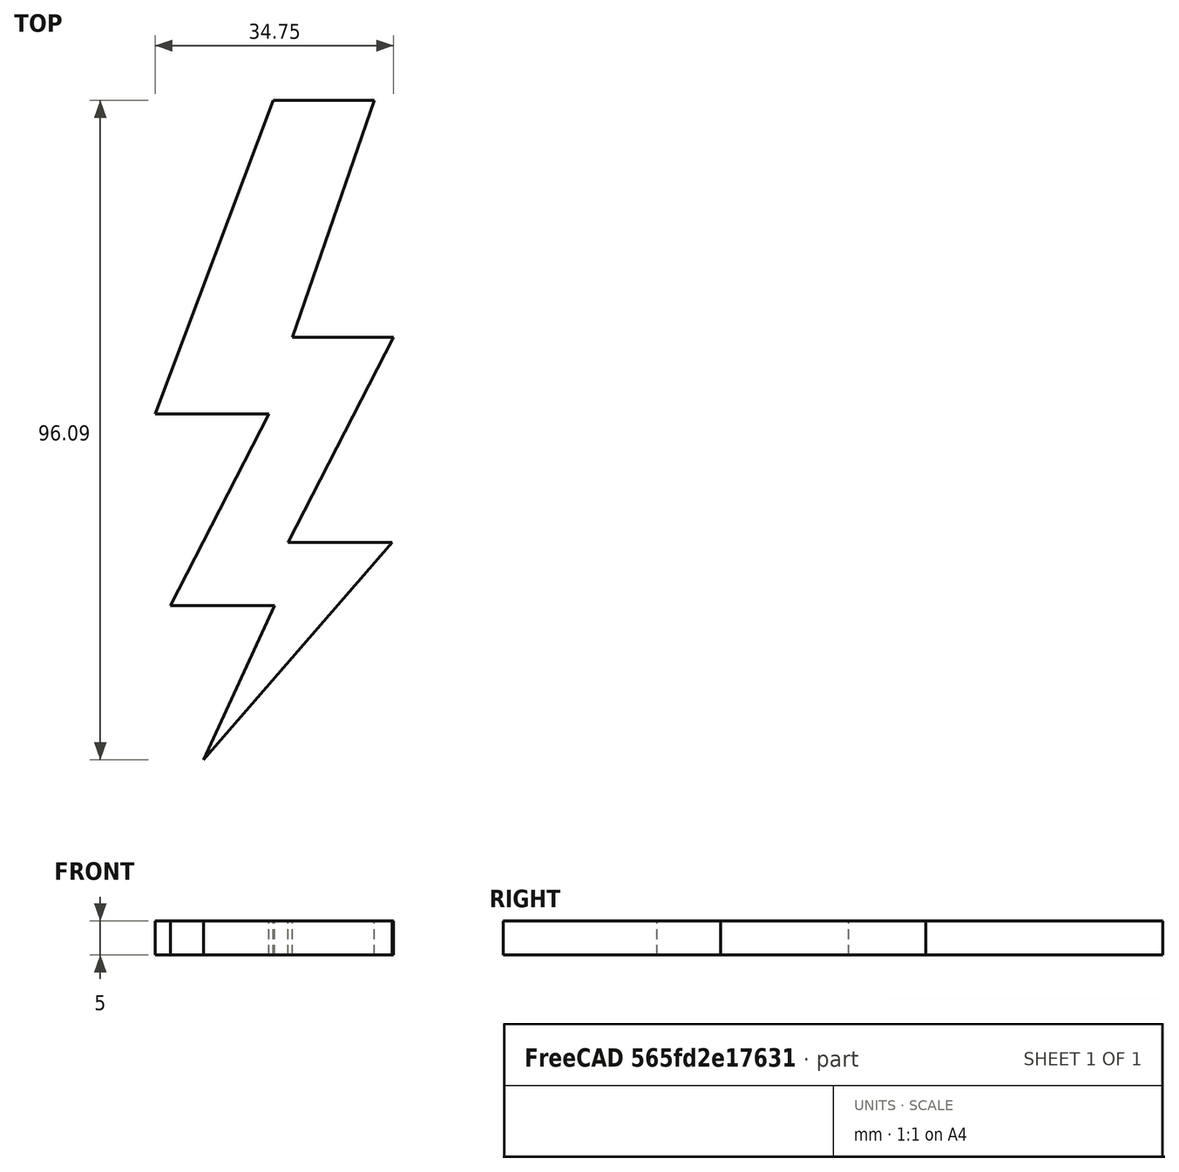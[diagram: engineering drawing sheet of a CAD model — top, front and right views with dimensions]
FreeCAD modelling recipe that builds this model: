
FCSTD DOCUMENT  (FreeCAD 0.21R33694 (Git))
Label: OJT1_T16R03.team_llamp
License: All rights reserved
LicenseURL: http://en.wikipedia.org/wiki/All_rights_reserved
objects: Sketcher::SketchObject×1, PartDesign::Pad×1, PartDesign::Body×1
note: 4 computed .brp shape members not serialized (recipe doc carries the construction recipe); baked Part::Feature solids carry a one-line shape summary decoded from their .brp

FEATURE [Sketcher::SketchObject] Sketch
  FullyConstrained = false
  MapMode = 5
  Support = -> [XY_Plane]
  sketch-geometry (11):
    g0: LineSegment StartX=20.152 StartY=49.243 StartZ=0 EndX=34.8878 EndY=49.243 EndZ=0
    g1: LineSegment StartX=34.8878 StartY=49.243 StartZ=0 EndX=22.9686 EndY=14.698 EndZ=0
    g2: LineSegment StartX=22.9686 StartY=14.698 StartZ=0 EndX=37.7161 EndY=14.698 EndZ=0
    g3: LineSegment StartX=37.7161 StartY=14.698 StartZ=0 EndX=22.3625 EndY=-15.201 EndZ=0
    g4: LineSegment StartX=22.3625 StartY=-15.201 StartZ=0 EndX=37.5184 EndY=-15.201 EndZ=0
    g5: LineSegment StartX=37.5184 StartY=-15.201 StartZ=0 EndX=10.0393 EndY=-46.847 EndZ=0
    g6: LineSegment StartX=10.0393 StartY=-46.847 StartZ=0 EndX=20.3423 EndY=-24.4228 EndZ=0
    g7: LineSegment StartX=20.3423 StartY=-24.4228 StartZ=0 EndX=5.19081 EndY=-24.4228 EndZ=0
    g8: LineSegment StartX=5.19081 StartY=-24.4228 StartZ=0 EndX=19.5388 EndY=3.51532 EndZ=0
    g9: LineSegment StartX=19.5388 StartY=3.51532 StartZ=0 EndX=2.97312 EndY=3.51532 EndZ=0
    g10: LineSegment StartX=2.97312 StartY=3.51532 StartZ=0 EndX=20.152 EndY=49.243 EndZ=0
  constraints (16):
    c: Horizontal(g0)
    c: Coincident(g0,g1)
    c: Coincident(g1,g2)
    c: Horizontal(g2)
    c: Coincident(g2,g3)
    c: Coincident(g3,g4)
    c: Horizontal(g4)
    c: Coincident(g4,g5)
    c: Coincident(g5,g6)
    c: Coincident(g6,g7)
    c: Horizontal(g7)
    c: Coincident(g7,g8)
    c: Coincident(g8,g9)
    c: Horizontal(g9)
    c: Coincident(g9,g10)
    c: Coincident(g10,g0)
FEATURE [PartDesign::Pad] Pad
  Direction = (0,0,1)
  Length = 5
  Length2 = 10
  Profile = -> Sketch
  ReferenceAxis = -> Sketch [N_Axis]
  Refine = true
  Type = 0
FEATURE [PartDesign::Body] Body
  Group = -> [Sketch,Pad]
  Origin = -> Origin
  Tip = -> Pad
